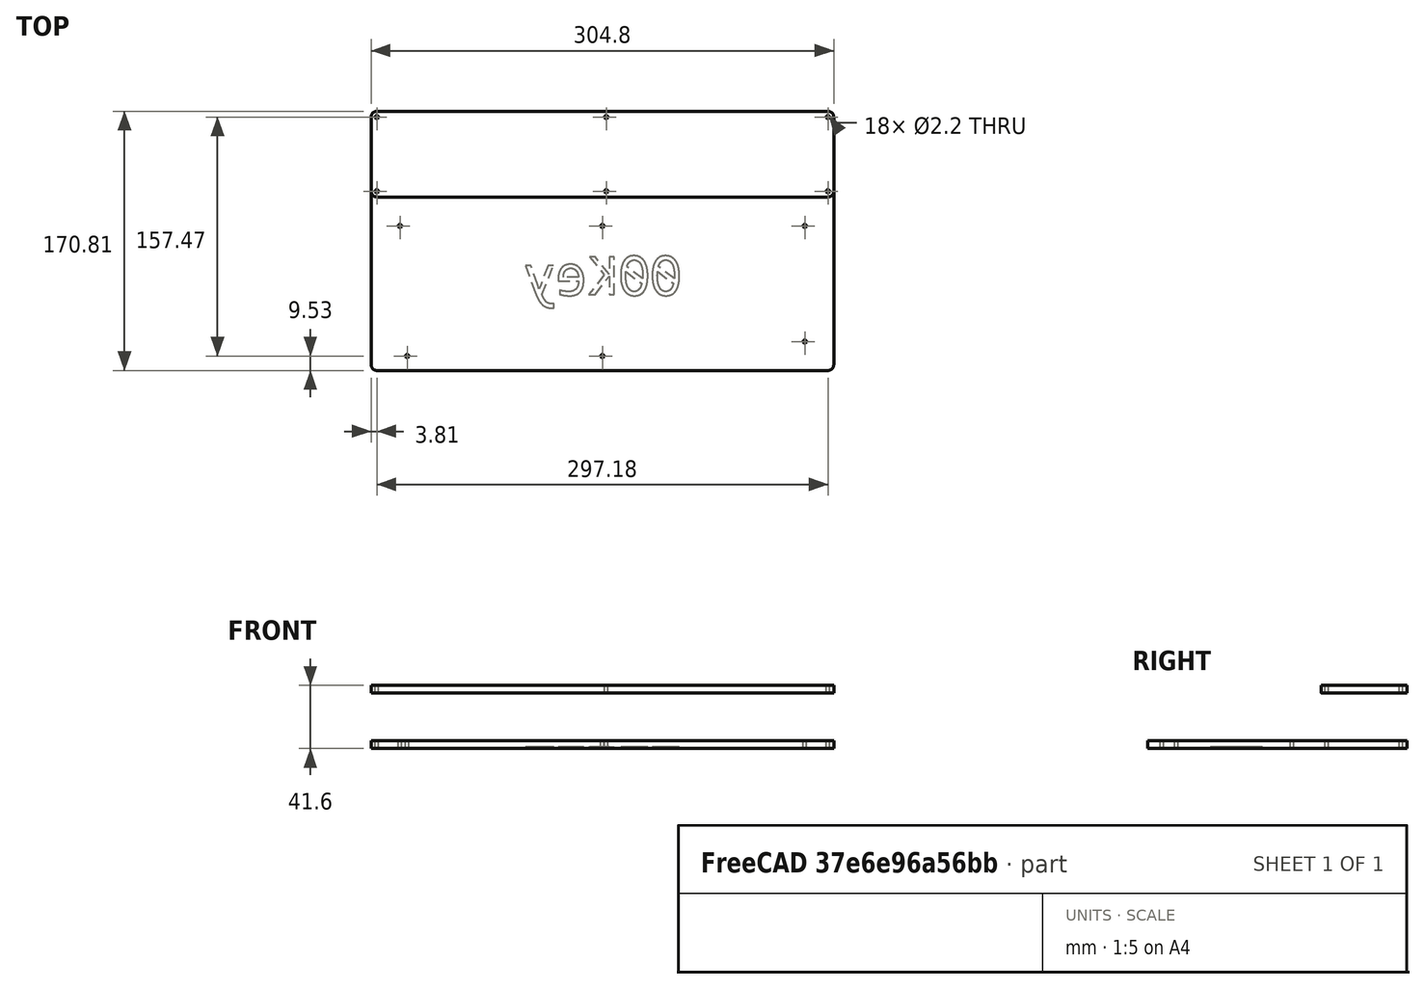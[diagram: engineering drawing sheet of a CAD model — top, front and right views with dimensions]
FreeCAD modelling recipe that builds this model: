
FCSTD DOCUMENT  (FreeCAD 0.18R4 (GitTag))
Label: plate
License: All rights reserved
LicenseURL: http://en.wikipedia.org/wiki/All_rights_reserved
objects: Part::Cylinder×18, Part::Feature×18, App::DocumentObjectGroup×7, Part::Box×2, Part::Fillet×2, Part::MultiFuse×2, Part::Cut×2, Part::Part2DObjectPython×2, Part::Extrusion×2, App::VRMLObject×1, Part::FeaturePython×1
note: 49 computed .brp shape members not serialized (recipe doc carries the construction recipe); baked Part::Feature solids carry a one-line shape summary decoded from their .brp

FEATURE [Part::Box] Box  label="Cube"
  AttacherType = Attacher::AttachEngine3D
  Height = 5
  Length = 304.8
  Width = 170.81
FEATURE [Part::Fillet] Fillet
  Base = -> Box
  Edges = 4 edges r=3.81: [Edge1,Edge3,Edge5,Edge7]
FEATURE [Part::Cylinder] Cylinder  label="HPTL"
  Angle = 360
  AttacherType = Attacher::AttachEngine3D
  Height = 5
  Placement = pos=(3.81,167,0) rot=(0,0,1;0rad)
  Radius = 1.1
FEATURE [Part::Cylinder] Cylinder001  label="HPTM"
  Angle = 360
  AttacherType = Attacher::AttachEngine3D
  Height = 5
  Placement = pos=(154.94,167,0) rot=(0,0,1;0rad)
  Radius = 1.1
FEATURE [Part::Cylinder] Cylinder002  label="HPTR"
  Angle = 360
  AttacherType = Attacher::AttachEngine3D
  Height = 5
  Placement = pos=(300.99,167,0) rot=(0,0,1;0rad)
  Radius = 1.1
FEATURE [Part::Cylinder] Cylinder003  label="HPBL"
  Angle = 360
  AttacherType = Attacher::AttachEngine3D
  Height = 5
  Placement = pos=(3.81,118.11,0) rot=(0,0,1;0rad)
  Radius = 1.1
FEATURE [Part::Cylinder] Cylinder004  label="HPBM"
  Angle = 360
  AttacherType = Attacher::AttachEngine3D
  Height = 5
  Placement = pos=(154.94,118.11,0) rot=(0,0,1;0rad)
  Radius = 1.1
FEATURE [Part::Cylinder] Cylinder005  label="HPBR"
  Angle = 360
  AttacherType = Attacher::AttachEngine3D
  Height = 5
  Placement = pos=(300.99,118.11,0) rot=(0,0,1;0rad)
  Radius = 1.1
FEATURE [Part::Cylinder] Cylinder006  label="HKTL"
  Angle = 360
  AttacherType = Attacher::AttachEngine3D
  Height = 5
  Placement = pos=(19.05,95.25,0) rot=(0,0,1;0rad)
  Radius = 1.1
FEATURE [Part::Cylinder] Cylinder007  label="HKTM"
  Angle = 360
  AttacherType = Attacher::AttachEngine3D
  Height = 5
  Placement = pos=(152.4,95.25,0) rot=(0,0,1;0rad)
  Radius = 1.1
FEATURE [Part::Cylinder] Cylinder008  label="HKTR"
  Angle = 360
  AttacherType = Attacher::AttachEngine3D
  Height = 5
  Placement = pos=(285.75,95.25,0) rot=(0,0,1;0rad)
  Radius = 1.1
FEATURE [Part::Cylinder] Cylinder009  label="HKBL"
  Angle = 360
  AttacherType = Attacher::AttachEngine3D
  Height = 5
  Placement = pos=(23.81,9.53,0) rot=(0,0,1;0rad)
  Radius = 1.1
FEATURE [Part::Cylinder] Cylinder010  label="HKBM"
  Angle = 360
  AttacherType = Attacher::AttachEngine3D
  Height = 5
  Placement = pos=(152.4,9.53,0) rot=(0,0,1;0rad)
  Radius = 1.1
FEATURE [Part::Cylinder] Cylinder011  label="HKBR"
  Angle = 360
  AttacherType = Attacher::AttachEngine3D
  Height = 5
  Placement = pos=(285.75,19.05,0) rot=(0,0,1;0rad)
  Radius = 1.1
FEATURE [Part::MultiFuse] Fusion
  Shapes = -> [Cylinder,Cylinder010,Cylinder009,Cylinder011,Cylinder008,Cylinder001,Cylinder002,Cylinder003,Cylinder004,Cylinder005,Cylinder006,Cylinder007]
FEATURE [Part::Cut] Cut
  Base = -> Fillet
  Tool = -> Fusion
FEATURE [App::VRMLObject] _0Key  label="PCB001"
  Placement = pos=(-39.7,211.13,15.8) rot=(0,0,1;0rad)
FEATURE [Part::Feature] Part__Feature  label="SPTL"
  Placement = pos=(3.81,167,5) rot=(0,0,1;0rad)
  shape: bbox 5.106 x 5.106 x 14 mm, 112 faces, 0 solids (baked)
  expr: Placement.Base.y = HPTL.Placement.Base.y
  expr: Placement.Base.x = HPTL.Placement.Base.x
FEATURE [Part::Feature] Part__Feature001  label="SPTM"
  Placement = pos=(154.94,167,5) rot=(0,0,1;0rad)
  shape: bbox 5.106 x 5.106 x 14 mm, 112 faces, 0 solids (baked)
  expr: Placement.Base.x = HPTM.Placement.Base.x
  expr: Placement.Base.y = HPTM.Placement.Base.y
FEATURE [App::DocumentObjectGroup] Group001  label="PCB"
  Group = -> [_0Key]
FEATURE [Part::Feature] Part__Feature002  label="SPTR"
  Placement = pos=(300.99,167,5) rot=(0,0,1;0rad)
  shape: bbox 5.106 x 5.106 x 14 mm, 112 faces, 0 solids (baked)
  expr: Placement.Base.y = HPTR.Placement.Base.y
  expr: Placement.Base.x = HPTR.Placement.Base.x
FEATURE [Part::Feature] Part__Feature003  label="SPBL"
  Placement = pos=(3.81,118.11,5) rot=(0,0,1;0rad)
  shape: bbox 5.106 x 5.106 x 14 mm, 112 faces, 0 solids (baked)
  expr: Placement.Base.x = HPBL.Placement.Base.x
  expr: Placement.Base.y = HPBL.Placement.Base.y
FEATURE [Part::Feature] Part__Feature004  label="SPBM"
  Placement = pos=(154.94,118.11,5) rot=(0,0,1;0rad)
  shape: bbox 5.106 x 5.106 x 14 mm, 112 faces, 0 solids (baked)
  expr: Placement.Base.x = HPBM.Placement.Base.x
  expr: Placement.Base.y = HPBM.Placement.Base.y
FEATURE [Part::Feature] Part__Feature005  label="SPBR"
  Placement = pos=(300.99,118.11,5) rot=(0,0,1;0rad)
  shape: bbox 5.106 x 5.106 x 14 mm, 112 faces, 0 solids (baked)
  expr: Placement.Base.x = HPBR.Placement.Base.x
  expr: Placement.Base.y = HPBR.Placement.Base.y
FEATURE [Part::Feature] Part__Feature006  label="SKTL"
  Placement = pos=(19.05,95.25,5) rot=(0,0,1;0rad)
  shape: bbox 5.106 x 5.106 x 14 mm, 112 faces, 0 solids (baked)
  expr: Placement.Base.x = HKTL.Placement.Base.x
  expr: Placement.Base.y = HKTL.Placement.Base.y
FEATURE [Part::Feature] Part__Feature007  label="SKTM"
  Placement = pos=(152.4,95.25,5) rot=(0,0,1;0rad)
  shape: bbox 5.106 x 5.106 x 14 mm, 112 faces, 0 solids (baked)
  expr: Placement.Base.x = HKTM.Placement.Base.x
  expr: Placement.Base.y = HKTM.Placement.Base.y
FEATURE [Part::Feature] Part__Feature008  label="SKTR"
  Placement = pos=(285.75,95.25,5) rot=(0,0,1;0rad)
  shape: bbox 5.106 x 5.106 x 14 mm, 112 faces, 0 solids (baked)
  expr: Placement.Base.x = HKTR.Placement.Base.x
  expr: Placement.Base.y = HKTR.Placement.Base.y
FEATURE [Part::Feature] Part__Feature009  label="SKBL"
  Placement = pos=(23.81,9.53,5) rot=(0,0,1;0rad)
  shape: bbox 5.106 x 5.106 x 14 mm, 112 faces, 0 solids (baked)
  expr: Placement.Base.x = HKBL.Placement.Base.x
  expr: Placement.Base.y = HKBL.Placement.Base.y
FEATURE [Part::Feature] Part__Feature010  label="SKBM"
  Placement = pos=(152.4,9.53,5) rot=(0,0,1;0rad)
  shape: bbox 5.106 x 5.106 x 14 mm, 112 faces, 0 solids (baked)
  expr: Placement.Base.x = HKBM.Placement.Base.x
  expr: Placement.Base.y = HKBM.Placement.Base.y
FEATURE [Part::Feature] Part__Feature011  label="SKBR"
  Placement = pos=(285.75,19.05,5) rot=(0,0,1;0rad)
  shape: bbox 5.106 x 5.106 x 14 mm, 112 faces, 0 solids (baked)
  expr: Placement.Base.x = HKBR.Placement.Base.x
  expr: Placement.Base.y = HKBR.Placement.Base.y
FEATURE [Part::Part2DObjectPython] ShapeString  label="00Key"  # Draft 2D object (typed FeaturePython)
  FontFile = <path>
  Placement = pos=(204.745,50,0) rot=(0,1,0;3.14159rad)
  Size = 30
  String = 00Key
  Tracking = 0
FEATURE [Part::Extrusion] Extrude
  Base = -> ShapeString
  Dir = (0,0,1)
  DirMode = 0
  FaceMakerClass = Part::FaceMakerBullseye
  LengthFwd = 1
  LengthRev = 0
  Solid = false
  Symmetric = false
FEATURE [Part::FeaturePython] XOR  label="XORBOTTOM"  # WARN: FeaturePython — macro-defined, semantics opaque (R4)
  Objects = -> [Extrude,Cut]
  Tolerance = 0
FEATURE [Part::Part2DObjectPython] Wire  # Draft 2D object (typed FeaturePython)
  ChamferSize = 0
  Closed = false
  End = (96.71,170.81,5)
  FilletRadius = 0
  Length = 116.38
  MakeFace = false
  Placement = pos=(208.09,170.81,0) rot=(0,0,1;0rad)
  Points = (4) [(0,0,0),(0,0,2.5),(-111.38,0,2.5),(-111.38,0,5)]
  Start = (208.09,170.81,0)
  Subdivisions = 0
FEATURE [Part::Extrusion] Extrude001  label="Split"
  Base = -> Wire
  Dir = (0,1,0)
  DirMode = 0
  FaceMakerClass = Part::FaceMakerBullseye
  LengthFwd = -170.81
  LengthRev = 0
  Solid = false
  Symmetric = false
FEATURE [App::DocumentObjectGroup] Group003  label="Bottom"
  Group = -> [XOR,Extrude001]
FEATURE [Part::Cylinder] Cylinder012  label="HPTL001"
  Angle = 360
  AttacherType = Attacher::AttachEngine3D
  Height = 5
  Placement = pos=(3.81,167,36.6) rot=(0,0,1;0rad)
  Radius = 1.1
FEATURE [Part::Box] Box001  label="Cube001"
  AttacherType = Attacher::AttachEngine3D
  Height = 5
  Length = 304.8
  Placement = pos=(0,114.31,36.6) rot=(0,0,1;0rad)
  Width = 56.5
FEATURE [Part::Fillet] Fillet001
  Base = -> Box001
  Edges = 4 edges r=3.81: [Edge1,Edge3,Edge5,Edge7]
FEATURE [Part::Cylinder] Cylinder013  label="HPTM001"
  Angle = 360
  AttacherType = Attacher::AttachEngine3D
  Height = 5
  Placement = pos=(154.94,167,36.6) rot=(0,0,1;0rad)
  Radius = 1.1
FEATURE [Part::Cylinder] Cylinder014  label="HPTR001"
  Angle = 360
  AttacherType = Attacher::AttachEngine3D
  Height = 5
  Placement = pos=(300.99,167,36.6) rot=(0,0,1;0rad)
  Radius = 1.1
FEATURE [Part::Cylinder] Cylinder015  label="HPBL001"
  Angle = 360
  AttacherType = Attacher::AttachEngine3D
  Height = 5
  Placement = pos=(3.81,118.11,36.6) rot=(0,0,1;0rad)
  Radius = 1.1
FEATURE [Part::Cylinder] Cylinder016  label="HPBM001"
  Angle = 360
  AttacherType = Attacher::AttachEngine3D
  Height = 5
  Placement = pos=(154.94,118.11,36.6) rot=(0,0,1;0rad)
  Radius = 1.1
FEATURE [Part::Cylinder] Cylinder017  label="HPBR001"
  Angle = 360
  AttacherType = Attacher::AttachEngine3D
  Height = 5
  Placement = pos=(300.99,118.11,36.6) rot=(0,0,1;0rad)
  Radius = 1.1
FEATURE [Part::MultiFuse] Fusion001
  Shapes = -> [Cylinder012,Cylinder013,Cylinder014,Cylinder015,Cylinder016,Cylinder017]
FEATURE [Part::Cut] Cut001
  Base = -> Fillet001
  Tool = -> Fusion001
FEATURE [App::DocumentObjectGroup] Group004  label="Top"
  Group = -> [Cut001]
FEATURE [Part::Feature] Part__Feature012  label="STL"
  Placement = pos=(3.81,167,16.6) rot=(0,0,1;0rad)
  shape: bbox 5.106 x 5.106 x 24 mm, 196 faces, 0 solids (baked)
  expr: Placement.Base.y = HPTL.Placement.Base.y
  expr: Placement.Base.x = HPTL.Placement.Base.x
FEATURE [App::DocumentObjectGroup] Group005  label="Standoffs Bottom"
  Group = -> [Part__Feature001,Part__Feature,Part__Feature002,Part__Feature003,Part__Feature004,Part__Feature005,Part__Feature006,Part__Feature007,Part__Feature008,Part__Feature009,Part__Feature010,Part__Feature011]
FEATURE [Part::Feature] Part__Feature013  label="STM"
  Placement = pos=(154.94,167,16.6) rot=(0,0,1;0rad)
  shape: bbox 5.106 x 5.106 x 24 mm, 196 faces, 0 solids (baked)
  expr: Placement.Base.y = HPTM.Placement.Base.y
  expr: Placement.Base.x = HPTM.Placement.Base.x
FEATURE [Part::Feature] Part__Feature014  label="STR"
  Placement = pos=(300.99,167,16.6) rot=(0,0,1;0rad)
  shape: bbox 5.106 x 5.106 x 24 mm, 196 faces, 0 solids (baked)
  expr: Placement.Base.y = HPTR.Placement.Base.y
  expr: Placement.Base.x = HPTR.Placement.Base.x
FEATURE [Part::Feature] Part__Feature015  label="SBL"
  Placement = pos=(3.81,118.11,16.6) rot=(0,0,1;0rad)
  shape: bbox 5.106 x 5.106 x 24 mm, 196 faces, 0 solids (baked)
  expr: Placement.Base.y = HPBL.Placement.Base.y
  expr: Placement.Base.x = HPBL.Placement.Base.x
FEATURE [Part::Feature] Part__Feature016  label="SBM"
  Placement = pos=(154.94,118.11,16.6) rot=(0,0,1;0rad)
  shape: bbox 5.106 x 5.106 x 24 mm, 196 faces, 0 solids (baked)
  expr: Placement.Base.y = HPBM.Placement.Base.y
  expr: Placement.Base.x = HPBM.Placement.Base.x
FEATURE [Part::Feature] Part__Feature017  label="SBR"
  Placement = pos=(300.99,118.11,16.6) rot=(0,0,1;0rad)
  shape: bbox 5.106 x 5.106 x 24 mm, 196 faces, 0 solids (baked)
  expr: Placement.Base.y = HPBR.Placement.Base.y
  expr: Placement.Base.x = HPBR.Placement.Base.x
FEATURE [App::DocumentObjectGroup] Group006  label="Standoffs Top"
  Group = -> [Part__Feature012,Part__Feature013,Part__Feature014,Part__Feature015,Part__Feature016,Part__Feature017]
FEATURE [App::DocumentObjectGroup] Group  label="Standoffs"
  Group = -> [Group005,Group006]
FEATURE [App::DocumentObjectGroup] Group002  label="Data"
  Group = -> [Group001,Group]
note: 1 file-system path scrubbed to <path> (originals preserved in the JSON sidecar)
